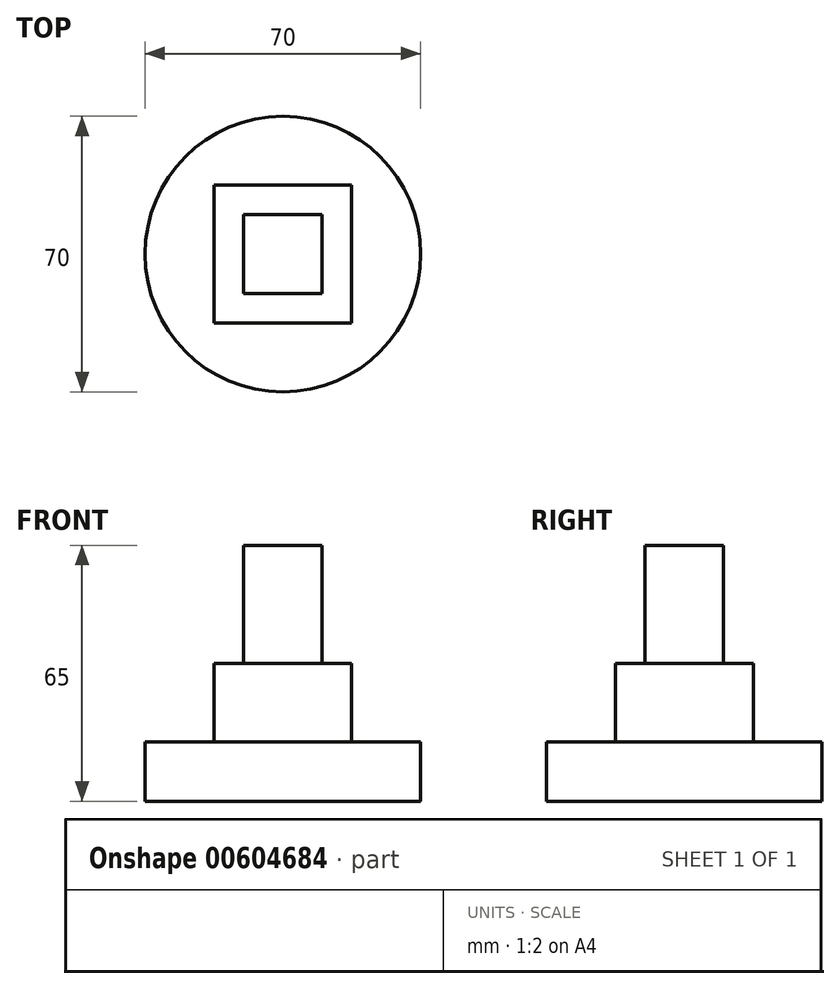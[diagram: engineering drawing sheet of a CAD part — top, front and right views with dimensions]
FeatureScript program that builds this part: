
annotation { "Feature Type Name" : "Feature", "Feature Type Description" : "" }
export const myFeature = defineFeature(function(context is Context, id is Id, definition is map)
    precondition{}
    {
        {
            var Q0;
            Q0=qCreatedBy(makeId("Top.planeOp"),FACE);
            var sketch = newSketch(context, id + "F0", { "sketchPlane" : qUnion([Q0])});
            skCircle(sketch, "E0", {"center": v(0, 0) * mm, "radius": 35 * mm});
            skSolve(sketch);
        }
        {
            var Q0;
            Q0=makeQuery(id+"F0.imprint","IMPRINT",FACE,{"disambiguationData":[TD([[makeQuery(id+"F0.imprint","IMPRINT",EDGE,{"derivedFrom":sQuery(id+"F0.wireOp",EDGE,"E0")}),1.0]])]});
            extrude(context, id + "F1", {"entities" : qUnion([Q0]), "depth" : 15 * mm, "offsetDistance" : 25.4 * mm});
        }
        {
            var Q0;
            Q0=makeQuery(id+"F1.opExtrude","CAP_FACE",FACE,{"disambiguationData":[OSD([sQuery(id+"F0.wireOp",EDGE,"E0")])],"isStart":false});
            var sketch = newSketch(context, id + "F2", { "sketchPlane" : qUnion([Q0])});
            skLineSegment(sketch, "E1.bottom", {"start": v(17.5, -17.5) * mm, "end": v(-17.5, -17.5) * mm});
            skLineSegment(sketch, "E1.top", {"start": v(17.5, 17.5) * mm, "end": v(-17.5, 17.5) * mm});
            skLineSegment(sketch, "E1.left", {"start": v(17.5, -17.5) * mm, "end": v(17.5, 17.5) * mm});
            skLineSegment(sketch, "E1.right", {"start": v(-17.5, -17.5) * mm, "end": v(-17.5, 17.5) * mm});
            skPoint(sketch, "E1.middle", {"position": v(0, 0) * mm});
            skSolve(sketch);
        }
        {
            var Q0;
            Q0 = qSketchRegion(id + "F2", true);
            extrude(context, id + "F3", {"entities" : qUnion([Q0]), "operationType" : NewBodyOperationType.ADD, "depth" : 20 * mm, "offsetDistance" : 25.4 * mm});
        }
        {
            var Q0;
            Q0=makeQuery(id+"F3.opExtrude","CAP_FACE",FACE,{"disambiguationData":[OSD([sQuery(id+"F2.wireOp",EDGE,"E1.bottom"),sQuery(id+"F2.wireOp",EDGE,"E1.top"),sQuery(id+"F2.wireOp",EDGE,"E1.left"),sQuery(id+"F2.wireOp",EDGE,"E1.right")])],"isStart":false});
            var sketch = newSketch(context, id + "F4", { "sketchPlane" : qUnion([Q0])});
            skLineSegment(sketch, "E2.bottom", {"start": v(10, -10) * mm, "end": v(-10, -10) * mm});
            skLineSegment(sketch, "E2.top", {"start": v(10, 10) * mm, "end": v(-10, 10) * mm});
            skLineSegment(sketch, "E2.left", {"start": v(10, -10) * mm, "end": v(10, 10) * mm});
            skLineSegment(sketch, "E2.right", {"start": v(-10, -10) * mm, "end": v(-10, 10) * mm});
            skPoint(sketch, "E2.middle", {"position": v(0, 0) * mm});
            skSolve(sketch);
        }
        {
            var Q0;
            Q0 = qSketchRegion(id + "F4", true);
            extrude(context, id + "F5", {"entities" : qUnion([Q0]), "operationType" : NewBodyOperationType.ADD, "depth" : 30 * mm, "offsetDistance" : 25.4 * mm});
        }
    });
